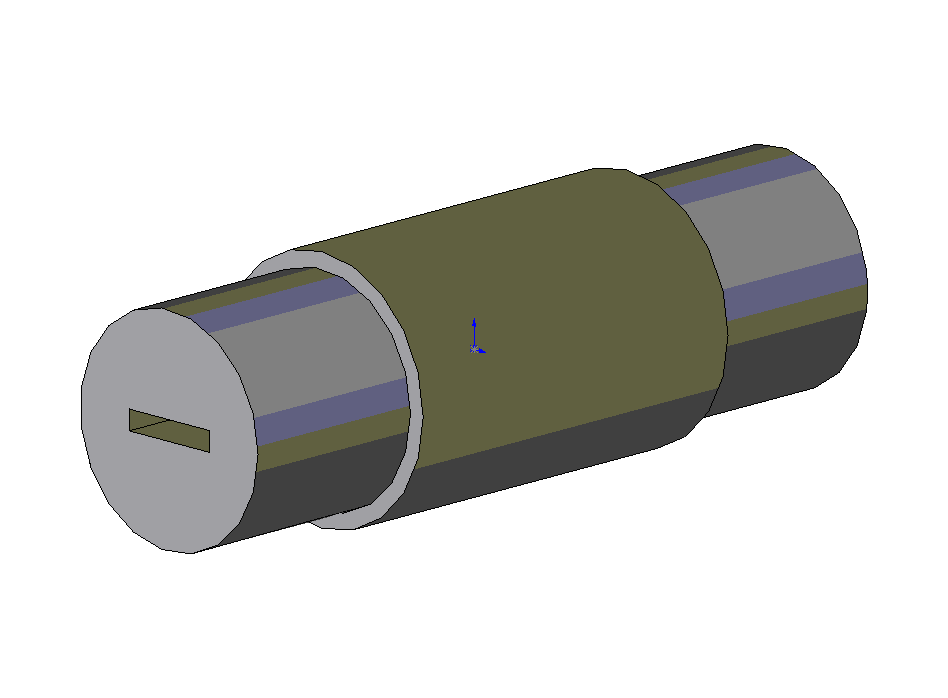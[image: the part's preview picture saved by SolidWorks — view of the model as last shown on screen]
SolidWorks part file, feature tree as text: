
SOLIDWORKS PART (.sldprt)
format: sldprt  version: not decoded by parser v0  size: 255,488 bytes
history: native  units: mm
features: sketch x3, cut_extrude x2, mirror x2, material x1, extrude x1 (+12 scaffold rows collapsed)
feature tree (21):
  scaffold x12  (default folders/planes/origin — collapsed)
  material  "Material <not specified>"
  sketch  "Sketch1"  dims[D1=25.4mm]
  extrude  "Base-Extrude"  Depth=76.2mm
  sketch  "Sketch2"  dims[D1=1.585mm]
  cut_extrude  "Cut-Extrude1"  Depth=19.05mm
  mirror  "Mirror1"
  sketch  "Sketch3"  dims[D1=2.0mm D2=10.0mm]
  cut_extrude  "Slot for Flat Blade Screw Driver"  Depth=6mm
  mirror  "Mirror2"
decode coverage: 6 of 8 modeling features carry decoded parameters
note: suppression state not decoded; provenance and decode notes live in map.json
